FCSTD DOCUMENT  (FreeCAD 0.19R24291 (Git))
Label: Right Panel
License: All rights reserved
LicenseURL: http://en.wikipedia.org/wiki/All_rights_reserved
objects: Sketcher::SketchObject×5, PartDesign::Body×5, TechDraw::DrawViewPart×4, TechDraw::DrawSVGTemplate×3, TechDraw::DrawPage×3, Mesh::Feature×1
note: 10 computed .brp shape members not serialized (recipe doc carries the construction recipe); baked Part::Feature solids carry a one-line shape summary decoded from their .brp

FEATURE [Sketcher::SketchObject] Sketch
  FullyConstrained = true
  MapMode = 5
  Support = -> [XY_Plane]
  sketch-geometry (24):
    g0: LineSegment StartX=0 StartY=0 StartZ=0 EndX=53 EndY=0 EndZ=0
    g1: LineSegment StartX=153 StartY=1e-16 StartZ=0 EndX=153 EndY=150 EndZ=0
    g2: LineSegment StartX=153 StartY=376 StartZ=0 EndX=0 EndY=376 EndZ=0
    g3: LineSegment StartX=0 StartY=376 StartZ=0 EndX=0 EndY=201 EndZ=0
    g4: LineSegment StartX=53 StartY=0 StartZ=0 EndX=53 EndY=-4 EndZ=0
    g5: LineSegment StartX=53 StartY=-4 StartZ=0 EndX=113 EndY=-4 EndZ=0
    g6: LineSegment StartX=113 StartY=-4 StartZ=0 EndX=113 EndY=0 EndZ=0
    g7: LineSegment StartX=113 StartY=0 StartZ=0 EndX=153 EndY=1e-16 EndZ=0
    g8: LineSegment StartX=153 StartY=150 StartZ=0 EndX=111 EndY=150 EndZ=0
    g9: LineSegment StartX=111 StartY=150 StartZ=0 EndX=111 EndY=162 EndZ=0
    g10: LineSegment StartX=153 StartY=250 StartZ=0 EndX=153 EndY=376 EndZ=0
    g11: LineSegment StartX=111 StartY=250 StartZ=0 EndX=153 EndY=250 EndZ=0
    g12: LineSegment StartX=111 StartY=162 StartZ=0 EndX=106 EndY=162 EndZ=0
    g13: LineSegment StartX=111 StartY=172 StartZ=0 EndX=106 EndY=172 EndZ=0
    g14: ArcOfCircle CenterX=106 CenterY=167 CenterZ=0 NormalX=0 NormalY=0 NormalZ=1 AngleXU=0 Radius=5 StartAngle=1.5708 EndAngle=4.71239
    g15: LineSegment StartX=111 StartY=172 StartZ=0 EndX=111 EndY=221 EndZ=0
    g16: LineSegment StartX=0 StartY=136 StartZ=0 EndX=3.2 EndY=136 EndZ=0
    g17: LineSegment StartX=3.2 StartY=136 StartZ=0 EndX=3.2 EndY=201 EndZ=0
    g18: LineSegment StartX=3.2 StartY=201 StartZ=0 EndX=0 EndY=201 EndZ=0
    g19: LineSegment StartX=0 StartY=136 StartZ=0 EndX=0 EndY=0 EndZ=0
    g20: LineSegment StartX=111 StartY=237 StartZ=0 EndX=99 EndY=237 EndZ=0
    g21: LineSegment StartX=111 StartY=221 StartZ=0 EndX=99 EndY=221 EndZ=0
    g22: ArcOfCircle CenterX=99 CenterY=229 CenterZ=0 NormalX=0 NormalY=0 NormalZ=1 AngleXU=0 Radius=8 StartAngle=1.5708 EndAngle=4.71239
    g23: LineSegment StartX=111 StartY=237 StartZ=0 EndX=111 EndY=250 EndZ=0
  constraints (68):
    c: Coincident(g7,g1)
    c: Coincident(g10,g2)
    c: Coincident(g2,g3)
    c: Coincident(g19,g0)
    c: Horizontal(g0)
    c: Horizontal(g2)
    c: Vertical(g1)
    c: Vertical(g3)
    c: Coincident(g0,g-1)
    c: DistanceX(g0,g7) = 153
    c: DistanceY(g19,g3) = 376
    c: Coincident(g4,g5)
    c: Horizontal(g5)
    c: Coincident(g5,g6)
    c: Vertical(g6)
    c: Vertical(g4)
    c: DistanceX(g0,g4) = 53
    c: DistanceX(g0,g6) = 113
    c: Coincident(g0,g4)
    c: Coincident(g7,g6)
    c: Tangent(g0,g7)
    c: Horizontal(g8)
    c: Coincident(g8,g9)
    c: Vertical(g9)
    c: DistanceY(g1,g8) = 150
    c: Coincident(g1,g8)
    c: Tangent(g1,g10)
    c: DistanceY(g4,g4) = 4
    c: Horizontal(g11)
    c: Coincident(g10,g11)
    c: DistanceX(g0,g11) = 111
    c: DistanceY(g1,g10) = 250
    c: Horizontal(g12)
    c: Horizontal(g13)
    c: Vertical(g13,g12)
    c: Coincident(g14,g13)
    c: Coincident(g14,g12)
    c: Coincident(g9,g12)
    c: Coincident(g15,g13)
    c: Tangent(g9,g15)
    c: DistanceY(g8,g9) = 12
    c: DistanceY(g9,g13) = 10
    c: Vertical(g14,g12)
    c: DistanceX(g14,g9) = 5
    c: Horizontal(g16)
    c: Coincident(g16,g17)
    c: Vertical(g17)
    c: Coincident(g17,g18)
    c: Horizontal(g18)
    c: DistanceX(g16,g16) = 3.2
    c: DistanceY(g17,g17) = 65
    c: Coincident(g3,g18)
    c: Coincident(g19,g16)
    c: Tangent(g3,g19)
    c: DistanceY(g4,g16) = 140
    c: Coincident(g11,g23)
    c: Horizontal(g20)
    c: Horizontal(g21)
    c: Coincident(g22,g21)
    c: Coincident(g22,g20)
    c: Coincident(g15,g21)
    c: Coincident(g23,g20)
    c: Tangent(g15,g23)
    c: DistanceY(g6,g20) = 237
    c: DistanceY(g15,g20) = 16
    c: DistanceX(g21,g21) = 12
    c: Equal(g21,g20)
    c: Angle(g22) = 3.14159
FEATURE [PartDesign::Body] Body  label="Deck Right"
  Group = -> [Sketch]
  Origin = -> Origin
FEATURE [Sketcher::SketchObject] Sketch001
  FullyConstrained = true
  MapMode = 5
  sketch-geometry (22):
    g0: LineSegment StartX=0 StartY=0 StartZ=0 EndX=53 EndY=0 EndZ=0
    g1: LineSegment StartX=153 StartY=0 StartZ=0 EndX=153 EndY=150 EndZ=0
    g2: LineSegment StartX=153 StartY=376 StartZ=0 EndX=0 EndY=376 EndZ=0
    g3: LineSegment StartX=0 StartY=376 StartZ=0 EndX=0 EndY=240 EndZ=0
    g4: LineSegment StartX=53 StartY=0 StartZ=0 EndX=53 EndY=-4 EndZ=0
    g5: LineSegment StartX=53 StartY=-4 StartZ=0 EndX=113 EndY=-4 EndZ=0
    g6: LineSegment StartX=113 StartY=-4 StartZ=0 EndX=113 EndY=0 EndZ=0
    g7: LineSegment StartX=113 StartY=3e-16 StartZ=0 EndX=153 EndY=0 EndZ=0
    g8: LineSegment StartX=153 StartY=150 StartZ=0 EndX=118 EndY=150 EndZ=0
    g9: LineSegment StartX=118 StartY=150 StartZ=0 EndX=118 EndY=155 EndZ=0
    g10: LineSegment StartX=153 StartY=250 StartZ=0 EndX=153 EndY=376 EndZ=0
    g11: LineSegment StartX=108 StartY=250 StartZ=0 EndX=153 EndY=250 EndZ=0
    g12: LineSegment StartX=118 StartY=155 StartZ=0 EndX=108 EndY=155 EndZ=0
    g13: LineSegment StartX=0 StartY=125 StartZ=0 EndX=17 EndY=125 EndZ=0
    g14: LineSegment StartX=17 StartY=125 StartZ=0 EndX=17 EndY=240 EndZ=0
    g15: LineSegment StartX=17 StartY=240 StartZ=0 EndX=0 EndY=240 EndZ=0
    g16: LineSegment StartX=0 StartY=125 StartZ=0 EndX=0 EndY=0 EndZ=0
    g17: LineSegment StartX=88 StartY=240 StartZ=0 EndX=108 EndY=240 EndZ=0
    g18: LineSegment StartX=108 StartY=240 StartZ=0 EndX=108 EndY=250 EndZ=0
    g19: LineSegment StartX=108 StartY=125 StartZ=0 EndX=88 EndY=125 EndZ=0
    g20: LineSegment StartX=88 StartY=125 StartZ=0 EndX=88 EndY=240 EndZ=0
    g21: LineSegment StartX=108 StartY=155 StartZ=0 EndX=108 EndY=125 EndZ=0
  constraints (61):
    c: Coincident(g7,g1)
    c: Coincident(g10,g2)
    c: Coincident(g2,g3)
    c: Coincident(g16,g0)
    c: Horizontal(g0)
    c: Horizontal(g2)
    c: Vertical(g1)
    c: Vertical(g3)
    c: Coincident(g0,g-1)
    c: DistanceX(g0,g7) = 153
    c: DistanceY(g16,g3) = 376
    c: Coincident(g4,g5)
    c: Horizontal(g5)
    c: Coincident(g5,g6)
    c: Vertical(g6)
    c: Vertical(g4)
    c: DistanceX(g0,g4) = 53
    c: DistanceX(g0,g6) = 113
    c: Coincident(g0,g4)
    c: Coincident(g7,g6)
    c: Tangent(g0,g7)
    c: Horizontal(g8)
    c: Coincident(g8,g9)
    c: Vertical(g9)
    c: DistanceY(g1,g8) = 150
    c: DistanceX(g8,g8) = 35
    c: Coincident(g1,g8)
    c: Tangent(g1,g10)
    c: DistanceY(g4,g4) = 4
    c: Horizontal(g11)
    c: Coincident(g10,g11)
    c: DistanceY(g1,g10) = 250
    c: Horizontal(g12)
    c: Coincident(g9,g12)
    c: DistanceY(g8,g9) = 5
    c: Horizontal(g13)
    c: Coincident(g13,g14)
    c: Vertical(g14)
    c: Coincident(g14,g15)
    c: Horizontal(g15)
    c: Coincident(g3,g15)
    c: Coincident(g16,g13)
    c: Tangent(g3,g16)
    c: DistanceY(g0,g13) = 125
    c: DistanceY(g0,g3) = 240
    c: DistanceX(g13,g13) = 17
    c: Coincident(g17,g18)
    c: Coincident(g21,g19)
    c: Coincident(g19,g20)
    c: Coincident(g20,g17)
    c: Horizontal(g17)
    c: Horizontal(g19)
    c: Vertical(g18)
    c: Vertical(g20)
    c: DistanceX(g19,g19) = 20
    c: Horizontal(g19,g13)
    c: Horizontal(g14,g17)
    c: DistanceX(g21,g1) = 45
    c: Coincident(g21,g12)
    c: Tangent(g18,g21)
    c: Coincident(g11,g18)
FEATURE [PartDesign::Body] Body001  label="Deck Left"
  Group = -> [Sketch001]
  Origin = -> Origin088
  Placement = pos=(0,0,0) rot=(0,1,0;3.14159rad)
FEATURE [Mesh::Feature] light_bar_x2
  Placement = pos=(0,0,0) rot=(0,0,1;0.785398rad)
FEATURE [TechDraw::DrawSVGTemplate] Template  label="<userpath>/AppData/Local/Temp/FreeCAD_Doc_c52be904-0459-40b6-a8d3-4737a9b002aa_916aa3_27340/Arch_C_Portrait.svg"
  Height = 609.6
  Orientation = 0
  Width = 457.2
  expr: Label = Template
FEATURE [Sketcher::SketchObject] Sketch002
  FullyConstrained = true
  MapMode = 5
  Support = -> [XY_Plane089]
  sketch-geometry (25):
    g0: LineSegment StartX=0 StartY=0 StartZ=0 EndX=53 EndY=0 EndZ=0
    g1: LineSegment StartX=153 StartY=0 StartZ=0 EndX=153 EndY=150 EndZ=0
    g2: LineSegment StartX=153 StartY=290 StartZ=0 EndX=0 EndY=290 EndZ=0
    g3: LineSegment StartX=0 StartY=290 StartZ=0 EndX=0 EndY=201 EndZ=0
    g4: LineSegment StartX=53 StartY=0 StartZ=0 EndX=53 EndY=-4 EndZ=0
    g5: LineSegment StartX=53 StartY=-4 StartZ=0 EndX=113 EndY=-4 EndZ=0
    g6: LineSegment StartX=113 StartY=-4 StartZ=0 EndX=113 EndY=0 EndZ=0
    g7: LineSegment StartX=113 StartY=0 StartZ=0 EndX=153 EndY=0 EndZ=0
    g8: LineSegment StartX=153 StartY=150 StartZ=0 EndX=118 EndY=150 EndZ=0
    g9: LineSegment StartX=118 StartY=150 StartZ=0 EndX=118 EndY=162 EndZ=0
    g10: LineSegment StartX=118 StartY=162 StartZ=0 EndX=108 EndY=162 EndZ=0
    g11: LineSegment StartX=118 StartY=172 StartZ=0 EndX=108 EndY=172 EndZ=0
    g12: ArcOfCircle CenterX=108 CenterY=167 CenterZ=0 NormalX=0 NormalY=0 NormalZ=1 AngleXU=0 Radius=5 StartAngle=1.5708 EndAngle=4.71239
    g13: LineSegment StartX=118 StartY=172 StartZ=0 EndX=118 EndY=212 EndZ=0
    g14: LineSegment StartX=0 StartY=136 StartZ=0 EndX=3.2 EndY=136 EndZ=0
    g15: LineSegment StartX=3.2 StartY=136 StartZ=0 EndX=3.2 EndY=201 EndZ=0
    g16: LineSegment StartX=3.2 StartY=201 StartZ=0 EndX=0 EndY=201 EndZ=0
    g17: LineSegment StartX=0 StartY=136 StartZ=0 EndX=0 EndY=0 EndZ=0
    g18: LineSegment StartX=118 StartY=212 StartZ=0 EndX=98 EndY=212 EndZ=0
    g19: ArcOfCircle CenterX=98 CenterY=231 CenterZ=0 NormalX=0 NormalY=0 NormalZ=1 AngleXU=0 Radius=19 StartAngle=1.5708 EndAngle=4.71239
    g20: Circle CenterX=20 CenterY=10 CenterZ=0 NormalX=0 NormalY=0 NormalZ=1 AngleXU=0 Radius=2.6
    g21: Circle CenterX=143 CenterY=10 CenterZ=0 NormalX=0 NormalY=0 NormalZ=1 AngleXU=0 Radius=2.6
    g22: Circle CenterX=143 CenterY=130 CenterZ=0 NormalX=0 NormalY=0 NormalZ=1 AngleXU=0 Radius=2.6
    g23: LineSegment StartX=98 StartY=250 StartZ=0 EndX=153 EndY=250 EndZ=0
    g24: LineSegment StartX=153 StartY=290 StartZ=0 EndX=153 EndY=250 EndZ=0
  constraints (73):
    c: Coincident(g7,g1)
    c: Coincident(g2,g3)
    c: Coincident(g17,g0)
    c: Horizontal(g0)
    c: Horizontal(g2)
    c: Vertical(g1)
    c: Vertical(g3)
    c: Coincident(g0,g-1)
    c: DistanceX(g0,g7) = 153
    c: DistanceY(g17,g3) = 290
    c: Coincident(g4,g5)
    c: Horizontal(g5)
    c: Coincident(g5,g6)
    c: Vertical(g6)
    c: Vertical(g4)
    c: DistanceX(g0,g4) = 53
    c: DistanceX(g0,g6) = 113
    c: Coincident(g0,g4)
    c: Coincident(g7,g6)
    c: Tangent(g0,g7)
    c: Horizontal(g8)
    c: Coincident(g8,g9)
    c: Vertical(g9)
    c: DistanceY(g1,g8) = 150
    c: Coincident(g1,g8)
    c: DistanceY(g4,g4) = 4
    c: Horizontal(g10)
    c: Horizontal(g11)
    c: Vertical(g11,g10)
    c: Coincident(g12,g11)
    c: Coincident(g12,g10)
    c: Coincident(g9,g10)
    c: Coincident(g13,g11)
    c: Tangent(g9,g13)
    c: DistanceY(g8,g9) = 12
    c: DistanceY(g9,g11) = 10
    c: Vertical(g12,g10)
    c: DistanceX(g12,g9) = 10
    c: Horizontal(g14)
    c: Coincident(g14,g15)
    c: Vertical(g15)
    c: Coincident(g15,g16)
    c: Horizontal(g16)
    c: DistanceX(g14,g14) = 3.2
    c: DistanceY(g15,g15) = 65
    c: Coincident(g3,g16)
    c: Coincident(g17,g14)
    c: Tangent(g3,g17)
    c: DistanceY(g4,g14) = 140
    c: Horizontal(g18)
    c: Coincident(g19,g18)
    c: Coincident(g13,g18)
    c: DistanceY(g6,g19) = 250
    c: DistanceX(g18,g18) = 20
    c: Angle(g19) = 3.14159
    c: DistanceY(g13,g13) = 40
    c: Vertical(g19,g18)
    c: Radius(g20) = 2.6
    c: Equal(g20,g21)
    c: DistanceY(g0,g20) = 10
    c: DistanceX(g0,g20) = 20
    c: Horizontal(g20,g21)
    c: DistanceX(g21,g1) = 10
    c: Equal(g20,g22) = 2.6
    c: DistanceX(g22,g1) = 10
    c: DistanceY(g22,g1) = 20
    c: DistanceY(g1,g13) = 212
    c: Tangent(g19,g23) = 1.5708
    c: DistanceX(g8,g8) = 35
    c: Vertical(g1,g23)
    c: Vertical(g23,g2)
    c: Coincident(g24,g2)
    c: Coincident(g24,g23)
FEATURE [TechDraw::DrawViewPart] View001
  CoarseView = false
  Direction = (0,0,1)
  Focus = 100
  HardHidden = false
  IsoCount = 0
  IsoHidden = false
  IsoVisible = false
  LockPosition = false
  Perspective = false
  Rotation = 0
  ScaleType = 0
  SeamHidden = false
  SeamVisible = true
  SmoothHidden = false
  SmoothVisible = true
  Source = -> [Sketch002]
  X = 180
  XDirection = (1,0,0)
  Y = 320
FEATURE [PartDesign::Body] Body002  label="Deck Right001"
  Group = -> [Sketch002]
  Origin = -> Origin089
FEATURE [Sketcher::SketchObject] Sketch003
  FullyConstrained = true
  MapMode = 5
  sketch-geometry (21):
    g0: LineSegment StartX=0 StartY=0 StartZ=0 EndX=53 EndY=0 EndZ=0
    g1: LineSegment StartX=153 StartY=0 StartZ=0 EndX=153 EndY=155 EndZ=0
    g2: LineSegment StartX=115 StartY=290 StartZ=0 EndX=0 EndY=290 EndZ=0
    g3: LineSegment StartX=0 StartY=290 StartZ=0 EndX=0 EndY=240 EndZ=0
    g4: LineSegment StartX=53 StartY=0 StartZ=0 EndX=53 EndY=-4 EndZ=0
    g5: LineSegment StartX=53 StartY=-4 StartZ=0 EndX=113 EndY=-4 EndZ=0
    g6: LineSegment StartX=113 StartY=-4 StartZ=0 EndX=113 EndY=0 EndZ=0
    g7: LineSegment StartX=113 StartY=0 StartZ=0 EndX=153 EndY=0 EndZ=0
    g8: LineSegment StartX=153 StartY=155 StartZ=0 EndX=108 EndY=155 EndZ=0
    g9: LineSegment StartX=0 StartY=125 StartZ=0 EndX=17 EndY=125 EndZ=0
    g10: LineSegment StartX=17 StartY=125 StartZ=0 EndX=17 EndY=240 EndZ=0
    g11: LineSegment StartX=17 StartY=240 StartZ=0 EndX=0 EndY=240 EndZ=0
    g12: LineSegment StartX=0 StartY=125 StartZ=0 EndX=0 EndY=0 EndZ=0
    g13: LineSegment StartX=88 StartY=240 StartZ=0 EndX=115 EndY=240 EndZ=0
    g14: LineSegment StartX=108 StartY=125 StartZ=0 EndX=88 EndY=125 EndZ=0
    g15: LineSegment StartX=88 StartY=125 StartZ=0 EndX=88 EndY=240 EndZ=0
    g16: LineSegment StartX=108 StartY=155 StartZ=0 EndX=108 EndY=125 EndZ=0
    g17: Circle CenterX=20 CenterY=10 CenterZ=0 NormalX=0 NormalY=0 NormalZ=1 AngleXU=0 Radius=2.6
    g18: Circle CenterX=143 CenterY=10 CenterZ=0 NormalX=0 NormalY=0 NormalZ=1 AngleXU=0 Radius=2.6
    g19: Circle CenterX=143 CenterY=135 CenterZ=0 NormalX=0 NormalY=0 NormalZ=1 AngleXU=0 Radius=2.6
    g20: LineSegment StartX=115 StartY=290 StartZ=0 EndX=115 EndY=240 EndZ=0
  constraints (60):
    c: Coincident(g7,g1)
    c: Coincident(g2,g3)
    c: Coincident(g12,g0)
    c: Horizontal(g0)
    c: Horizontal(g2)
    c: Vertical(g1)
    c: Vertical(g3)
    c: Coincident(g0,g-1)
    c: DistanceX(g0,g7) = 153
    c: DistanceY(g12,g3) = 290
    c: Coincident(g4,g5)
    c: Horizontal(g5)
    c: Coincident(g5,g6)
    c: Vertical(g6)
    c: Vertical(g4)
    c: DistanceX(g0,g4) = 53
    c: DistanceX(g0,g6) = 113
    c: Coincident(g0,g4)
    c: Coincident(g7,g6)
    c: Tangent(g0,g7)
    c: Horizontal(g8)
    c: DistanceY(g1,g8) = 155
    c: Coincident(g1,g8)
    c: DistanceY(g4,g4) = 4
    c: Horizontal(g9)
    c: Coincident(g9,g10)
    c: Vertical(g10)
    c: Coincident(g10,g11)
    c: Horizontal(g11)
    c: Coincident(g3,g11)
    c: Coincident(g12,g9)
    c: Tangent(g3,g12)
    c: DistanceY(g0,g9) = 125
    c: DistanceY(g0,g3) = 240
    c: DistanceX(g9,g9) = 17
    c: Coincident(g16,g14)
    c: Coincident(g14,g15)
    c: Coincident(g15,g13)
    c: Horizontal(g13)
    c: Horizontal(g14)
    c: Vertical(g15)
    c: DistanceX(g14,g14) = 20
    c: Horizontal(g14,g9)
    c: Horizontal(g10,g13)
    c: DistanceX(g16,g1) = 45
    c: Radius(g17) = 2.6
    c: DistanceX(g0,g17) = 20
    c: DistanceY(g0,g17) = 10
    c: Equal(g17,g18)
    c: Equal(g18,g19)
    c: Horizontal(g17,g18)
    c: Vertical(g19,g18)
    c: DistanceY(g19,g1) = 20
    c: DistanceX(g19,g1) = 10
    c: Coincident(g8,g16)
    c: DistanceX(g2,g2) = 115
    c: Vertical(g2,g13)
    c: Coincident(g20,g2)
    c: Coincident(g20,g13)
    c: DistanceX(g8,g8) = 45
FEATURE [TechDraw::DrawViewPart] View
  CoarseView = false
  Direction = (0,0,1)
  Focus = 100
  HardHidden = false
  IsoCount = 0
  IsoHidden = false
  IsoVisible = false
  LockPosition = false
  Perspective = false
  Rotation = 0
  ScaleType = 0
  SeamHidden = false
  SeamVisible = true
  SmoothHidden = false
  SmoothVisible = true
  Source = -> [Sketch003]
  X = 350
  XDirection = (1,0,0)
  Y = 320
FEATURE [TechDraw::DrawPage] Page
  KeepUpdated = true
  NextBalloonIndex = 1
  ProjectionType = 0
  Template = -> Template
  Views = -> [View,View001]
FEATURE [PartDesign::Body] Body003  label="Deck Left001"
  Group = -> [Sketch003]
  Origin = -> Origin090
  Placement = pos=(0,0,0) rot=(0,1,0;3.14159rad)
FEATURE [Sketcher::SketchObject] Sketch004
  FullyConstrained = false
  MapMode = 5
  Support = -> [XY_Plane091]
  sketch-geometry (43):
    g0: LineSegment StartX=0 StartY=0 StartZ=0 EndX=155 EndY=0 EndZ=0
    g1: LineSegment StartX=190 StartY=25 StartZ=0 EndX=190 EndY=235 EndZ=0
    g2: LineSegment StartX=190 StartY=235 StartZ=0 EndX=0 EndY=235 EndZ=0
    g3: LineSegment StartX=0 StartY=235 StartZ=0 EndX=0 EndY=70 EndZ=0
    g4: LineSegment StartX=10 StartY=20 StartZ=0 EndX=30 EndY=20 EndZ=0
    g5: LineSegment StartX=40 StartY=30 StartZ=0 EndX=40 EndY=50 EndZ=0
    g6: LineSegment StartX=30 StartY=60 StartZ=0 EndX=10 EndY=60 EndZ=0
    g7: LineSegment StartX=0 StartY=10 StartZ=0 EndX=0 EndY=0 EndZ=0
    g8: ArcOfCircle CenterX=10 CenterY=10 CenterZ=0 NormalX=0 NormalY=0 NormalZ=1 AngleXU=0 Radius=10 StartAngle=1.5708 EndAngle=3.14159
    g9: ArcOfCircle CenterX=30 CenterY=30 CenterZ=0 NormalX=0 NormalY=0 NormalZ=1 AngleXU=0 Radius=10 StartAngle=4.71239 EndAngle=6.28319
    g10: ArcOfCircle CenterX=30 CenterY=50 CenterZ=0 NormalX=0 NormalY=0 NormalZ=1 AngleXU=0 Radius=10 StartAngle=0 EndAngle=1.5708
    g11: ArcOfCircle CenterX=10 CenterY=70 CenterZ=0 NormalX=0 NormalY=0 NormalZ=1 AngleXU=0 Radius=10 StartAngle=3.14159 EndAngle=4.71239
    g12: Circle CenterX=10 CenterY=10 CenterZ=0 NormalX=0 NormalY=0 NormalZ=1 AngleXU=0 Radius=2.6
    g13: Circle CenterX=145 CenterY=10 CenterZ=0 NormalX=0 NormalY=0 NormalZ=1 AngleXU=0 Radius=2.6
    g14: LineSegment StartX=155 StartY=0 StartZ=0 EndX=155 EndY=25 EndZ=0
    g15: LineSegment StartX=155 StartY=25 StartZ=0 EndX=190 EndY=25 EndZ=0
    g16: Circle CenterX=10 CenterY=80 CenterZ=0 NormalX=0 NormalY=0 NormalZ=1 AngleXU=0 Radius=2.6
    g17: Circle CenterX=10 CenterY=215 CenterZ=0 NormalX=0 NormalY=0 NormalZ=1 AngleXU=0 Radius=2.6
    g18: Circle CenterX=180 CenterY=45 CenterZ=0 NormalX=0 NormalY=0 NormalZ=1 AngleXU=0 Radius=2.6
    g19: Circle CenterX=180 CenterY=215 CenterZ=0 NormalX=0 NormalY=0 NormalZ=1 AngleXU=0 Radius=2.6
    g20: LineSegment StartX=110 StartY=0 StartZ=0 EndX=110 EndY=131.643 EndZ=0
    g21: LineSegment StartX=190 StartY=80 StartZ=0 EndX=45.2964 EndY=80 EndZ=0
    g22: ArcOfCircle CenterX=95 CenterY=80 CenterZ=0 NormalX=0 NormalY=0 NormalZ=1 AngleXU=0 Radius=5 StartAngle=1.5708 EndAngle=4.71239
    g23: ArcOfCircle CenterX=125 CenterY=80 CenterZ=0 NormalX=0 NormalY=0 NormalZ=1 AngleXU=0 Radius=5 StartAngle=4.71239 EndAngle=7.85398
    g24: LineSegment StartX=95 StartY=75 StartZ=0 EndX=125 EndY=75 EndZ=0
    g25: LineSegment StartX=95 StartY=85 StartZ=0 EndX=125 EndY=85 EndZ=0
    g26: ArcOfCircle CenterX=95 CenterY=95 CenterZ=0 NormalX=0 NormalY=0 NormalZ=1 AngleXU=0 Radius=5 StartAngle=1.5708 EndAngle=4.71239
    g27: ArcOfCircle CenterX=125 CenterY=95 CenterZ=0 NormalX=0 NormalY=0 NormalZ=1 AngleXU=0 Radius=5 StartAngle=4.71239 EndAngle=7.85398
    g28: LineSegment StartX=95 StartY=90 StartZ=0 EndX=125 EndY=90 EndZ=0
    g29: LineSegment StartX=95 StartY=100 StartZ=0 EndX=125 EndY=100 EndZ=0
    g30: ArcOfCircle CenterX=95 CenterY=50 CenterZ=0 NormalX=0 NormalY=0 NormalZ=1 AngleXU=0 Radius=5 StartAngle=1.5708 EndAngle=4.71239
    g31: ArcOfCircle CenterX=125 CenterY=50 CenterZ=0 NormalX=0 NormalY=0 NormalZ=1 AngleXU=0 Radius=5 StartAngle=4.71239 EndAngle=7.85398
    g32: LineSegment StartX=95 StartY=45 StartZ=0 EndX=125 EndY=45 EndZ=0
    g33: LineSegment StartX=95 StartY=55 StartZ=0 EndX=125 EndY=55 EndZ=0
    g34: ArcOfCircle CenterX=95 CenterY=65 CenterZ=0 NormalX=0 NormalY=0 NormalZ=1 AngleXU=0 Radius=5 StartAngle=1.5708 EndAngle=4.71239
    g35: ArcOfCircle CenterX=125 CenterY=65 CenterZ=0 NormalX=0 NormalY=0 NormalZ=1 AngleXU=0 Radius=5 StartAngle=4.71239 EndAngle=7.85398
    g36: LineSegment StartX=95 StartY=60 StartZ=0 EndX=125 EndY=60 EndZ=0
    g37: LineSegment StartX=95 StartY=70 StartZ=0 EndX=125 EndY=70 EndZ=0
    g38: ArcOfCircle CenterX=95 CenterY=110 CenterZ=0 NormalX=0 NormalY=0 NormalZ=1 AngleXU=0 Radius=5 StartAngle=1.5708 EndAngle=4.71239
    g39: ArcOfCircle CenterX=125 CenterY=110 CenterZ=0 NormalX=0 NormalY=0 NormalZ=1 AngleXU=0 Radius=5 StartAngle=4.71239 EndAngle=7.85398
    g40: LineSegment StartX=95 StartY=105 StartZ=0 EndX=125 EndY=105 EndZ=0
    g41: LineSegment StartX=95 StartY=115 StartZ=0 EndX=125 EndY=115 EndZ=0
    g42: Circle CenterX=180 CenterY=100 CenterZ=0 NormalX=0 NormalY=0 NormalZ=1 AngleXU=0 Radius=2.6
  constraints (112):
    c: Coincident(g1,g2)
    c: Coincident(g2,g3)
    c: Coincident(g7,g0)
    c: Horizontal(g0)
    c: Horizontal(g2)
    c: Vertical(g1)
    c: Vertical(g3)
    c: Coincident(g0,g-1)
    c: DistanceX(g2,g2) = 190
    c: Horizontal(g4)
    c: Vertical(g5)
    c: Horizontal(g6)
    c: Tangent(g3,g7)
    c: Tangent(g7,g8) = -1.5708
    c: Tangent(g4,g8) = 1.5708
    c: Tangent(g4,g9) = -1.5708
    c: Tangent(g5,g9) = -1.5708
    c: Tangent(g5,g10) = -1.5708
    c: Tangent(g6,g10) = -1.5708
    c: Tangent(g6,g11) = 1.5708
    c: Tangent(g3,g11) = -1.5708
    c: Radius(g8) = 10
    c: Equal(g8,g9)
    c: Equal(g9,g10)
    c: Equal(g10,g11)
    c: DistanceY(g0,g4) = 20
    c: DistanceX(g0,g5) = 40
    c: DistanceY(g0,g6) = 60
    c: Coincident(g12,g8)
    c: Horizontal(g13,g8)
    c: Radius(g12) = 2.6
    c: Equal(g12,g13)
    c: Vertical(g14)
    c: Coincident(g14,g15)
    c: Horizontal(g15)
    c: Coincident(g0,g14)
    c: DistanceX(g0,g0) = 155
    c: Coincident(g1,g15)
    c: DistanceY(g0,g1) = 235
    c: DistanceY(g14,g14) = 25
    c: DistanceX(g13,g0) = 10
    c: Equal(g12,g16) = 2.6
    c: Equal(g12,g17) = 2.6
    c: Equal(g12,g18) = 2.6
    c: Equal(g12,g19) = 2.6
    c: DistanceY(g17,g2) = 20
    c: Vertical(g17,g16)
    c: Vertical(g16,g8)
    c: DistanceY(g6,g16) = 20
    c: Horizontal(g17,g19)
    c: Vertical(g18,g19)
    c: DistanceY(g1,g18) = 20
    c: DistanceX(g19,g1) = 10
    c: PointOnObject(g20,g0)
    c: Vertical(g20)
    c: PointOnObject(g21,g1)
    c: Horizontal(g21)
    c: DistanceY(g0,g21) = 80
    c: DistanceX(g20,g1) = 80
    c: Tangent(g22,g25) = 1.5708
    c: Tangent(g22,g24) = -1.5708
    c: Tangent(g24,g23) = -1.5708
    c: Tangent(g25,g23) = 1.5708
    c: Horizontal(g24)
    c: Equal(g22,g23)
    c: PointOnObject(g22,g21)
    c: DistanceY(g22,g22) = 10
    c: Distance(g22,g20) = 15
    c: Distance(g23,g20) = 15
    c: Tangent(g26,g29) = 1.5708
    c: Tangent(g26,g28) = -1.5708
    c: Tangent(g28,g27) = -1.5708
    c: Tangent(g29,g27) = 1.5708
    c: Horizontal(g28)
    c: Equal(g26,g27)
    c: Equal(g22,g26) = 10
    c: Vertical(g26,g22)
    c: Vertical(g27,g23)
    c: DistanceY(g22,g26) = 5
    c: Tangent(g30,g33) = 1.5708
    c: Tangent(g30,g32) = -1.5708
    c: Tangent(g32,g31) = -1.5708
    c: Tangent(g33,g31) = 1.5708
    c: Horizontal(g32)
    c: Equal(g30,g31)
    c: Equal(g22,g30) = 10
    c: Tangent(g34,g37) = 1.5708
    c: Tangent(g34,g36) = -1.5708
    c: Tangent(g36,g35) = -1.5708
    c: Tangent(g37,g35) = 1.5708
    c: Horizontal(g36)
    c: Equal(g34,g35)
    c: Equal(g30,g34) = 10
    c: Vertical(g34,g30)
    c: Vertical(g35,g31)
    c: DistanceY(g30,g34) = 5
    c: Vertical(g30,g22)
    c: Vertical(g23,g35)
    c: DistanceY(g35,g23) = 5
    c: Tangent(g38,g41) = 1.5708
    c: Tangent(g38,g40) = -1.5708
    c: Tangent(g40,g39) = -1.5708
    c: Tangent(g41,g39) = 1.5708
    c: Horizontal(g40)
    c: Equal(g38,g39)
    c: Equal(g22,g38) = 10
    c: Vertical(g38,g26)
    c: Vertical(g39,g27)
    c: DistanceY(g26,g38) = 5
    c: DistanceY(g0,g42) = 100
    c: Vertical(g18,g42)
    c: Equal(g12,g42)
FEATURE [PartDesign::Body] Body004
  Group = -> [Sketch004]
  Origin = -> Origin091
FEATURE [TechDraw::DrawSVGTemplate] Template001
  Height = 297
  Orientation = 0
  Width = 210
FEATURE [TechDraw::DrawViewPart] View002
  CoarseView = false
  Direction = (0,0,1)
  Focus = 100
  HardHidden = false
  IsoCount = 0
  IsoHidden = false
  IsoVisible = false
  LockPosition = false
  Perspective = false
  Rotation = 0
  ScaleType = 0
  SeamHidden = false
  SeamVisible = true
  SmoothHidden = false
  SmoothVisible = true
  Source = -> [Sketch002]
  X = 105
  XDirection = (1,0,0)
  Y = 148.5
FEATURE [TechDraw::DrawPage] Page001
  KeepUpdated = true
  NextBalloonIndex = 1
  ProjectionType = 0
  Template = -> Template001
  Views = -> [View002]
FEATURE [TechDraw::DrawSVGTemplate] Template002
  Height = 297
  Orientation = 0
  Width = 210
FEATURE [TechDraw::DrawViewPart] View003
  CoarseView = false
  Direction = (0,0,1)
  Focus = 100
  HardHidden = false
  IsoCount = 0
  IsoHidden = false
  IsoVisible = false
  LockPosition = false
  Perspective = false
  Rotation = 0
  ScaleType = 0
  SeamHidden = false
  SeamVisible = true
  SmoothHidden = false
  SmoothVisible = true
  Source = -> [Sketch003]
  X = 105
  XDirection = (1,0,0)
  Y = 148.5
FEATURE [TechDraw::DrawPage] Page002
  KeepUpdated = true
  NextBalloonIndex = 1
  ProjectionType = 0
  Template = -> Template002
  Views = -> [View003]
